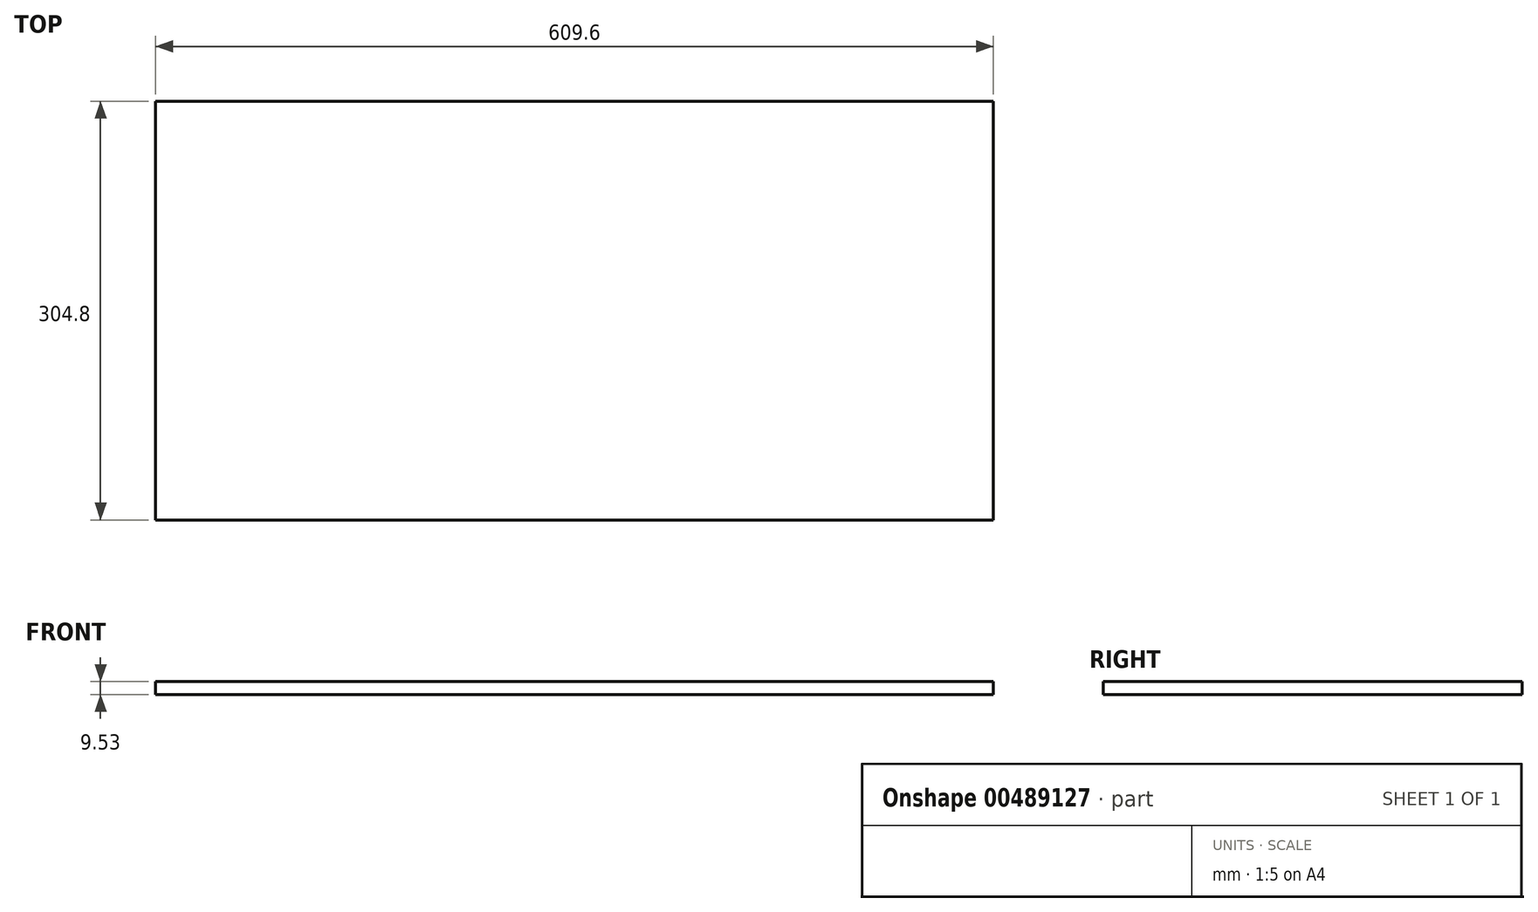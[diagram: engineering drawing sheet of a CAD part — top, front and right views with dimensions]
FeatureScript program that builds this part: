
annotation { "Feature Type Name" : "Feature", "Feature Type Description" : "" }
export const myFeature = defineFeature(function(context is Context, id is Id, definition is map)
    precondition{}
    {
        {
            var Q0;
            Q0=qCreatedBy(makeId("Top.planeOp"),FACE);
            var sketch = newSketch(context, id + "F0", { "sketchPlane" : qUnion([Q0])});
            skLineSegment(sketch, "E0.bottom", {"start": v(0, 0) * mm, "end": v(-609.6, 0) * mm});
            skLineSegment(sketch, "E0.top", {"start": v(0, 304.8) * mm, "end": v(-609.6, 304.8) * mm});
            skLineSegment(sketch, "E0.left", {"start": v(0, 0) * mm, "end": v(0, 304.8) * mm});
            skLineSegment(sketch, "E0.right", {"start": v(-609.6, 0) * mm, "end": v(-609.6, 304.8) * mm});
            skSolve(sketch);
        }
        {
            var Q0;
            Q0=makeQuery(id+"F0.imprint","IMPRINT",FACE,{"disambiguationData":[TD([[makeQuery(id+"F0.imprint","IMPRINT",EDGE,{"derivedFrom":sQuery(id+"F0.wireOp",EDGE,"E0.bottom")}),-1.0]])]});
            extrude(context, id + "F1", {"entities" : qUnion([Q0]), "depth" : 9.52 * mm});
        }
    });
